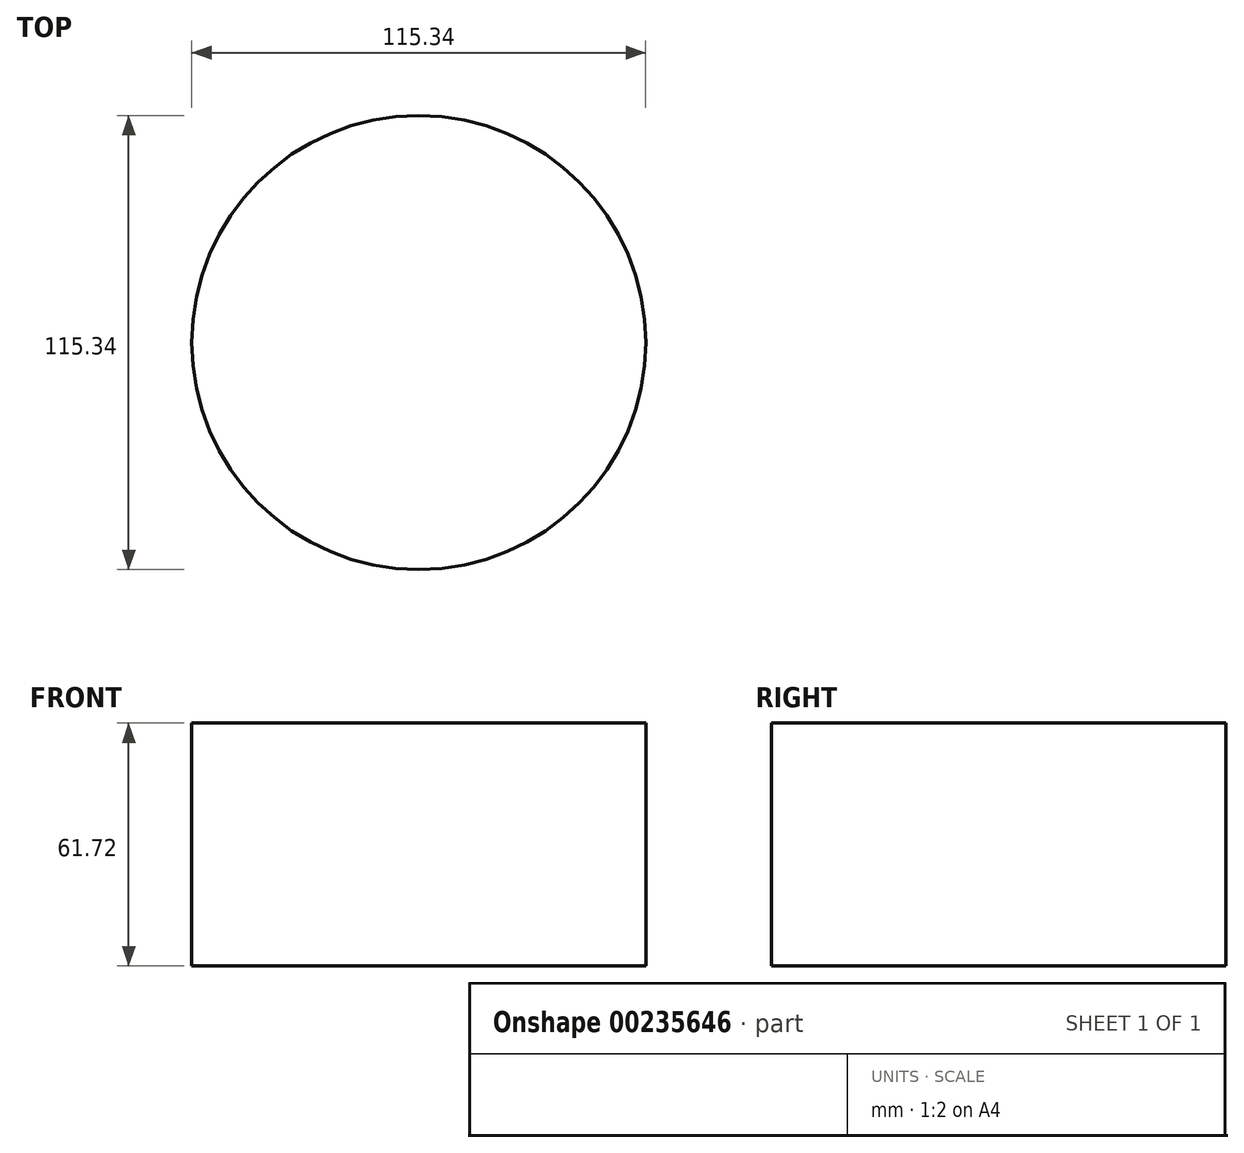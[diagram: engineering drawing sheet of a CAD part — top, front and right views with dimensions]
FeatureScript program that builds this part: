
annotation { "Feature Type Name" : "Feature", "Feature Type Description" : "" }
export const myFeature = defineFeature(function(context is Context, id is Id, definition is map)
    precondition{}
    {
        {
            var Q0;
            Q0=qCreatedBy(makeId("Top.planeOp"),FACE);
            var sketch = newSketch(context, id + "F0", { "sketchPlane" : qUnion([Q0])});
            skCircle(sketch, "E0", {"center": v(0, 0) * mm, "radius": 57.67 * mm});
            skSolve(sketch);
        }
        {
            var Q0;
            Q0 = qSketchRegion(id + "F0", true);
            extrude(context, id + "F1", {"entities" : qUnion([Q0]), "depth" : 61.72 * mm});
        }
    });
